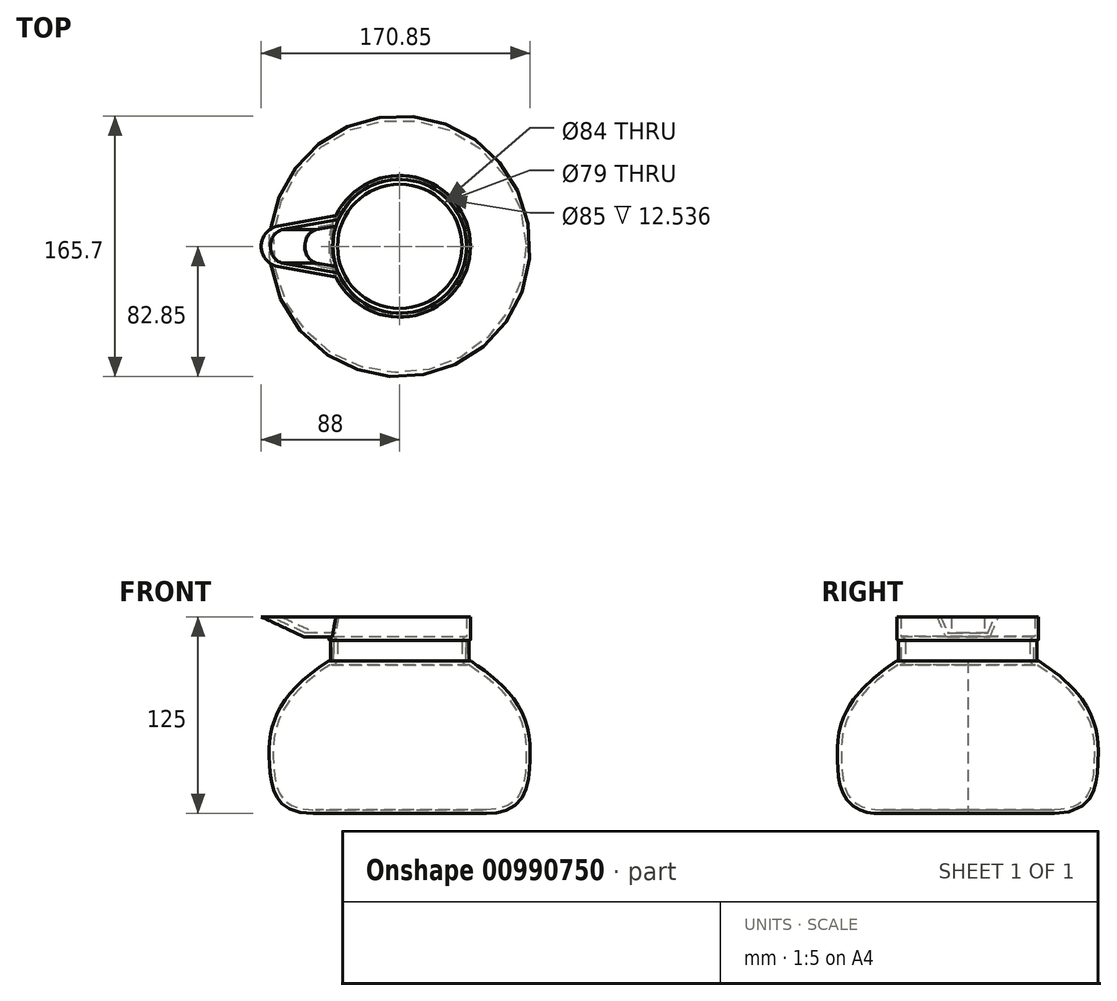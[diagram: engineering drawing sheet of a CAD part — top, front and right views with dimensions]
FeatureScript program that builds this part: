
annotation { "Feature Type Name" : "Feature", "Feature Type Description" : "" }
export const myFeature = defineFeature(function(context is Context, id is Id, definition is map)
    precondition{}
    {
        {
            var Q0;
            Q0=qCreatedBy(makeId("Front.planeOp"),FACE);
            var sketch = newSketch(context, id + "F0", { "sketchPlane" : qUnion([Q0])});
            skLineSegment(sketch, "E0", {"start": v(55, 0) * mm, "end": v(0, 0) * mm});
            skLineSegment(sketch, "E1", {"start": v(0, 0) * mm, "end": v(0, 125) * mm});
            skLineSegment(sketch, "E2", {"start": v(0, 125) * mm, "end": v(45, 125) * mm});
            skLineSegment(sketch, "E3", {"start": v(45, 125) * mm, "end": v(45, 110) * mm});
            skLineSegment(sketch, "E4", {"start": v(45, 110) * mm, "end": v(42, 110) * mm});
            skLineSegment(sketch, "E5", {"start": v(42, 110) * mm, "end": v(42, 97) * mm});
            skLineSegment(sketch, "E6", {"start": v(42, 97) * mm, "end": v(45, 97) * mm});
            skFitSpline(sketch, "E7", {"points": [v(45, 97) * mm, v(78.6, 61.92) * mm, v(82.55, 29.51) * mm, v(55, 0) * mm], "startDerivative": vector(147.58, -94.77) * mm, "endDerivative": vector(-216.75, 0) * mm});
            skSolve(sketch);
        }
        {
            var Q0;
            Q0 = qSketchRegion(id + "F0", true);
            var Q1;
            Q1=sQuery(id+"F0.wireOp",EDGE,"E1");
            revolve(context, id + "F1", {"surfaceOperationType" : NewSurfaceOperationType.NEW, "entities" : qUnion([Q0]), "axis" : qUnion([Q1]), "revolveType" : RevolveType.FULL});
        }
        {
            var Q0;
            Q0=makeQuery(id+"F1.opRevolve","SWEPT_EDGE",EDGE,{"disambiguationData":[OSD([sQuery(id+"F0.wireOp",EDGE,"E3"),sQuery(id+"F0.wireOp",EDGE,"E4")])]});
            var Q1;
            Q1=makeQuery(id+"F1.opRevolve","SWEPT_EDGE",EDGE,{"disambiguationData":[OSD([sQuery(id+"F0.wireOp",EDGE,"E4"),sQuery(id+"F0.wireOp",EDGE,"E5")])]});
            fillet(context, id + "F2", {"entities" : qUnion([Q0, Q1]), "radius" : 1 * mm, "tangentPropagation" : true, "allowEdgeOverflow" : false});
        }
        {
            var Q0;
            Q0=makeQuery(id+"F1.opRevolve","SWEPT_EDGE",EDGE,{"disambiguationData":[OSD([sQuery(id+"F0.wireOp",EDGE,"E5"),sQuery(id+"F0.wireOp",EDGE,"E6")])]});
            var Q1;
            Q1=makeQuery(id+"F1.opRevolve","SWEPT_FACE",FACE,{"disambiguationData":[OSD([sQuery(id+"F0.wireOp",EDGE,"E7")])]});
            fillet(context, id + "F3", {"entities" : qUnion([Q0, Q1]), "radius" : 1 * mm, "tangentPropagation" : true, "allowEdgeOverflow" : false});
        }
        {
            var Q0;
            Q0=qCreatedBy(makeId("Front.planeOp"),FACE);
            var sketch = newSketch(context, id + "F4", { "sketchPlane" : qUnion([Q0])});
            skArc(sketch, "E8", {"start": v(44, 109) * mm, "mid": v(43, 110) * mm, "end": v(42, 109) * mm});
            skLineSegment(sketch, "E9", {"start": v(42, 109) * mm, "end": v(42, 98) * mm});
            skArc(sketch, "E10", {"start": v(42, 98) * mm, "mid": v(43, 97) * mm, "end": v(44, 98) * mm});
            skLineSegment(sketch, "E11", {"start": v(44, 109) * mm, "end": v(44, 98) * mm});
            skSolve(sketch);
        }
        {
            var Q0;
            Q0 = qSketchRegion(id + "F4", true);
            var Q1;
            Q1=makeQuery(id+"F1.opRevolve","SWEPT_EDGE",EDGE,{"disambiguationData":[OSD([sQuery(id+"F0.wireOp",EDGE,"E2"),sQuery(id+"F0.wireOp",EDGE,"E3")])]});
            revolve(context, id + "F5", {"surfaceOperationType" : NewSurfaceOperationType.NEW, "entities" : qUnion([Q0]), "axis" : qUnion([Q1]), "revolveType" : RevolveType.FULL});
        }
        {
            var Q0;
            Q0=makeQuery(id+"F1.opRevolve","SWEPT_FACE",FACE,{"disambiguationData":[OSD([sQuery(id+"F0.wireOp",EDGE,"E2")])]});
            var sketch = newSketch(context, id + "F6", { "sketchPlane" : qUnion([Q0])});
            skArc(sketch, "E12", {"start": v(-88, 0) * mm, "mid": v(-84.99, -8.32) * mm, "end": v(-77.35, -12.79) * mm});
            skLineSegment(sketch, "E13", {"start": v(-77.35, -12.79) * mm, "end": v(0, -27) * mm});
            skLineSegment(sketch, "E14", {"start": v(0, -27) * mm, "end": v(0, 0) * mm});
            skArc(sketch, "E15.MirrorCS", {"start": v(-88, 0) * mm, "mid": v(-84.99, 8.32) * mm, "end": v(-77.35, 12.79) * mm});
            skLineSegment(sketch, "E16.MirrorCS", {"start": v(-77.35, 12.79) * mm, "end": v(0, 27) * mm});
            skLineSegment(sketch, "E17.MirrorCS", {"start": v(0, 27) * mm, "end": v(0, 0) * mm});
            skSolve(sketch);
        }
        {
            var Q0;
            Q0=qCreatedBy(makeId("Front.planeOp"),FACE);
            var sketch = newSketch(context, id + "F7", { "sketchPlane" : qUnion([Q0])});
            skLineSegment(sketch, "E18", {"start": v(0, 125) * mm, "end": v(27.19, 112.32) * mm});
            skSolve(sketch);
        }
        {
            var Q0;
            Q0 = qSketchRegion(id + "F6", true);
            var Q1;
            Q1 = qConstructionFilter(qBodyType(qCreatedBy(id + "F7" ,EDGE), BodyType.WIRE), ConstructionObject.NO);
            sweep(context, id + "F8", {"operationType" : NewBodyOperationType.ADD, "profiles" : qUnion([Q0]), "path" : qUnion([Q1])});
        }
        {
            var Q0;
            Q0=makeQuery(id+"F8.boolean.opBoolean","MERGE",FACE,{"derivedFrom":[makeQuery(id+"F1.opRevolve","SWEPT_FACE",FACE,{"disambiguationData":[OSD([sQuery(id+"F0.wireOp",EDGE,"E2")])]}),makeQuery(id+"F8.opSweep","CAP_FACE",FACE,{"disambiguationData":[OSD([sQuery(id+"F6.wireOp",EDGE,"E12"),sQuery(id+"F6.wireOp",EDGE,"E13"),sQuery(id+"F6.wireOp",EDGE,"E14"),sQuery(id+"F6.wireOp",EDGE,"E15.MirrorCS"),sQuery(id+"F6.wireOp",EDGE,"E16.MirrorCS"),sQuery(id+"F6.wireOp",EDGE,"E17.MirrorCS"),sQuery(id+"F7.wireOp",VERTEX,"E18.start")])],"isStart":true})]});
            shell(context, id + "F9", {"entities" : qUnion([Q0]), "thickness" : 2.5 * mm});
        }
    });
